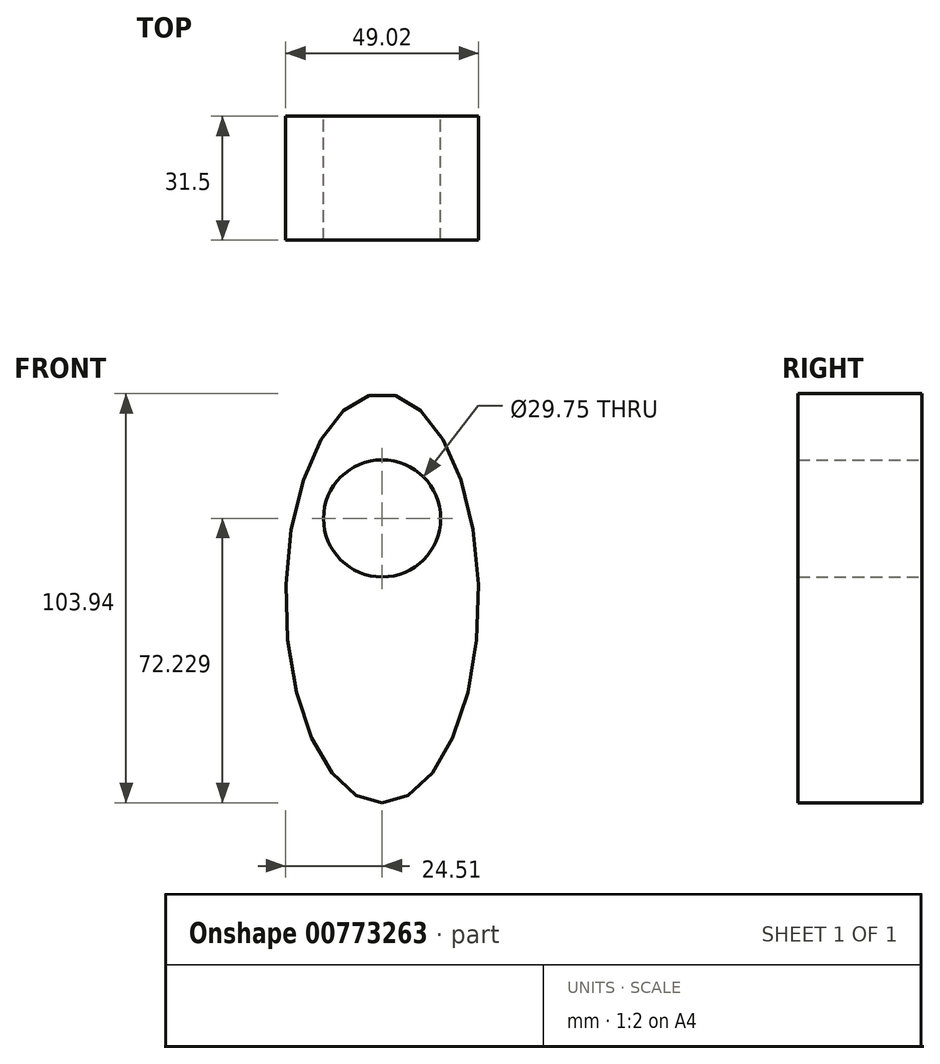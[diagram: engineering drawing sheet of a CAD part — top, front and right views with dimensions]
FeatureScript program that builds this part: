
annotation { "Feature Type Name" : "Feature", "Feature Type Description" : "" }
export const myFeature = defineFeature(function(context is Context, id is Id, definition is map)
    precondition{}
    {
        {
            var Q0;
            Q0=qCreatedBy(makeId("Front.planeOp"),FACE);
            var sketch = newSketch(context, id + "F0", { "sketchPlane" : qUnion([Q0])});
            skPoint(sketch, "E0", {"position": v(0, 0) * mm});
            skEllipse(sketch, "E1", {"center": v(0, 0) * mm, "majorRadius": 51.97 * mm, "minorRadius": 24.51 * mm, "majorAxis": v(0, -1)});
            skCircle(sketch, "E2", {"center": v(0, 20.26) * mm, "radius": 14.87 * mm});
            skSolve(sketch);
        }
        {
            var Q0;
            Q0 = qSketchRegion(id + "F0", true);
            extrude(context, id + "F1", {"entities" : qUnion([Q0]), "depth" : 31.5 * mm, "offsetDistance" : 25.4 * mm});
        }
    });
